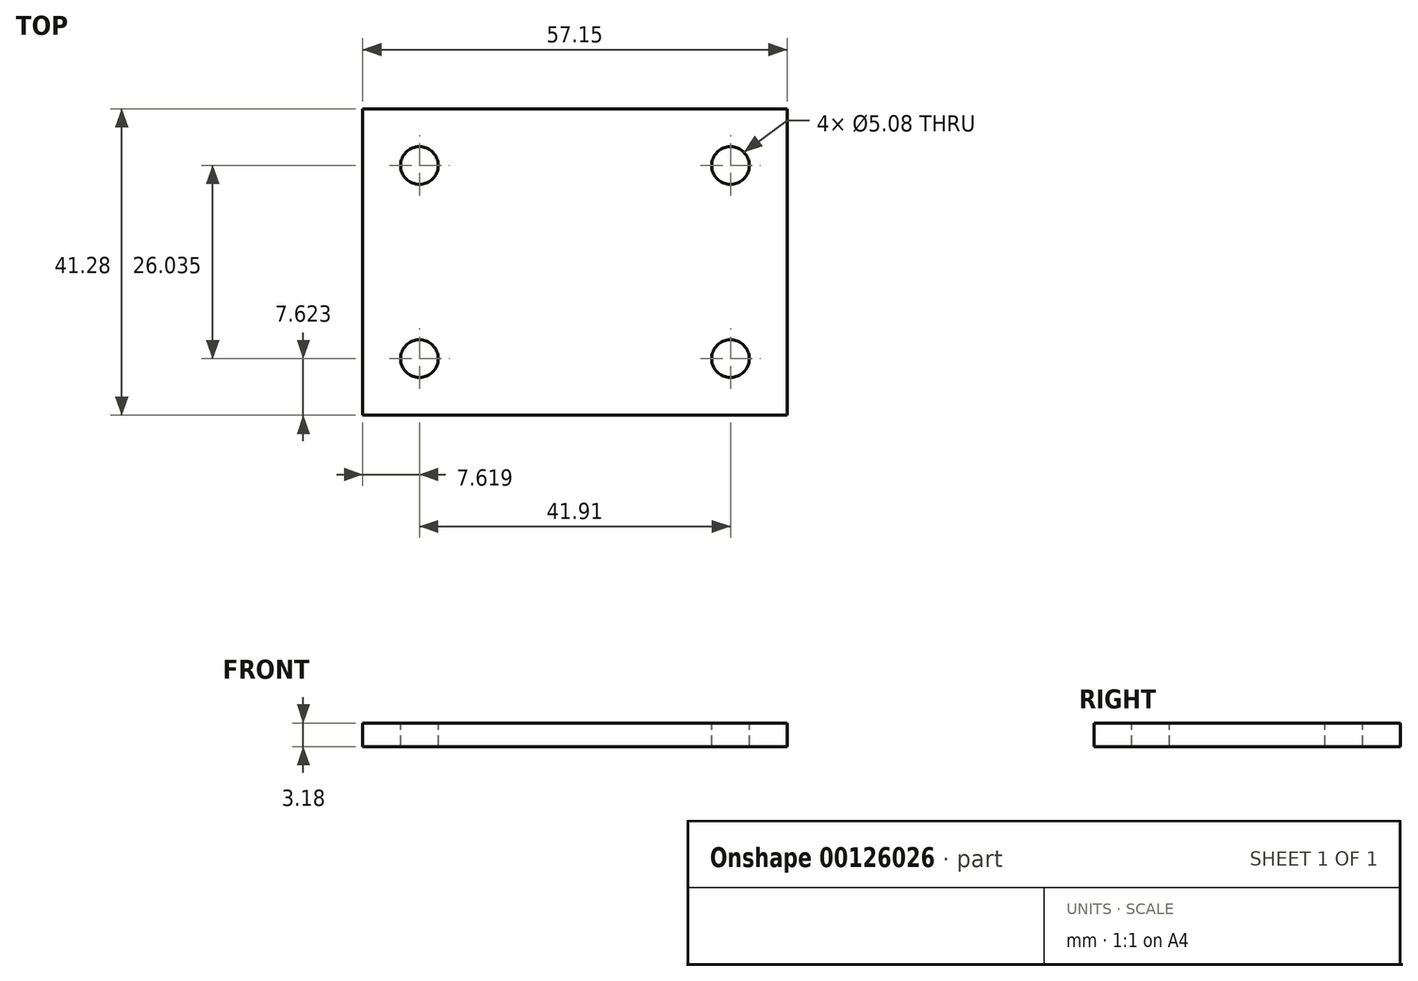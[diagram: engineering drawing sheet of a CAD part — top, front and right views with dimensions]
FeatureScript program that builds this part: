
annotation { "Feature Type Name" : "Feature", "Feature Type Description" : "" }
export const myFeature = defineFeature(function(context is Context, id is Id, definition is map)
    precondition{}
    {
        {
            var Q0;
            Q0=qCreatedBy(makeId("Top.planeOp"),FACE);
            var sketch = newSketch(context, id + "F0", { "sketchPlane" : qUnion([Q0])});
            skLineSegment(sketch, "E0.bottom", {"start": v(-24.2, 2.93) * mm, "end": v(32.96, 2.93) * mm});
            skLineSegment(sketch, "E0.top", {"start": v(-24.2, -38.35) * mm, "end": v(32.96, -38.35) * mm});
            skLineSegment(sketch, "E0.left", {"start": v(-24.2, 2.93) * mm, "end": v(-24.2, -38.35) * mm});
            skLineSegment(sketch, "E0.right", {"start": v(32.96, 2.93) * mm, "end": v(32.96, -38.35) * mm});
            skSolve(sketch);
        }
        {
            var Q0;
            Q0 = qSketchRegion(id + "F0", true);
            extrude(context, id + "F1", {"entities" : qUnion([Q0]), "depth" : 3.17 * mm});
        }
        {
            var Q0;
            Q0=makeQuery(id+"F1.opExtrude","CAP_FACE",FACE,{"disambiguationData":[OSD([sQuery(id+"F0.wireOp",EDGE,"E0.bottom"),sQuery(id+"F0.wireOp",EDGE,"E0.top"),sQuery(id+"F0.wireOp",EDGE,"E0.left"),sQuery(id+"F0.wireOp",EDGE,"E0.right")])],"isStart":false});
            var sketch = newSketch(context, id + "F2", { "sketchPlane" : qUnion([Q0])});
            skLineSegment(sketch, "E1.bottom", {"start": v(-24.2, 2.93) * mm, "end": v(-16.57, 2.93) * mm});
            skLineSegment(sketch, "E1.top", {"start": v(-24.2, -4.7) * mm, "end": v(-16.57, -4.7) * mm});
            skLineSegment(sketch, "E1.left", {"start": v(-24.2, 2.93) * mm, "end": v(-24.2, -4.7) * mm});
            skLineSegment(sketch, "E1.right", {"start": v(-16.57, 2.93) * mm, "end": v(-16.57, -4.7) * mm});
            skLineSegment(sketch, "E2.bottom", {"start": v(32.96, 2.93) * mm, "end": v(25.34, 2.93) * mm});
            skLineSegment(sketch, "E2.top", {"start": v(32.96, -4.7) * mm, "end": v(25.34, -4.7) * mm});
            skLineSegment(sketch, "E2.left", {"start": v(32.96, 2.93) * mm, "end": v(32.96, -4.7) * mm});
            skLineSegment(sketch, "E2.right", {"start": v(25.34, 2.93) * mm, "end": v(25.34, -4.7) * mm});
            skLineSegment(sketch, "E3.bottom", {"start": v(32.96, -38.35) * mm, "end": v(25.34, -38.35) * mm});
            skLineSegment(sketch, "E3.top", {"start": v(32.96, -30.73) * mm, "end": v(25.34, -30.73) * mm});
            skLineSegment(sketch, "E3.left", {"start": v(32.96, -38.35) * mm, "end": v(32.96, -30.73) * mm});
            skLineSegment(sketch, "E3.right", {"start": v(25.34, -38.35) * mm, "end": v(25.34, -30.73) * mm});
            skLineSegment(sketch, "E4.bottom", {"start": v(-24.2, -38.35) * mm, "end": v(-16.57, -38.35) * mm});
            skLineSegment(sketch, "E4.top", {"start": v(-24.2, -30.73) * mm, "end": v(-16.57, -30.73) * mm});
            skLineSegment(sketch, "E4.left", {"start": v(-24.2, -38.35) * mm, "end": v(-24.2, -30.73) * mm});
            skLineSegment(sketch, "E4.right", {"start": v(-16.57, -38.35) * mm, "end": v(-16.57, -30.73) * mm});
            skCircle(sketch, "E5", {"center": v(-16.57, -4.7) * mm, "radius": 2.54 * mm});
            skCircle(sketch, "E6", {"center": v(25.34, -4.7) * mm, "radius": 2.54 * mm});
            skCircle(sketch, "E7", {"center": v(25.34, -30.73) * mm, "radius": 2.54 * mm});
            skCircle(sketch, "E8", {"center": v(-16.57, -30.73) * mm, "radius": 2.54 * mm});
            skSolve(sketch);
        }
        {
            var Q0;
            {var subQ0=sQuery(id+"F2.wireOp",EDGE,"E1.right");var subQ1=sQuery(id+"F2.wireOp",EDGE,"E1.top");var subQ2=makeQuery(id+"F2.imprint","INTERSECT",VERTEX,{"derivedFrom":[subQ1,subQ0]});Q0=makeQuery(id+"F2.imprint","IMPRINT",FACE,{"disambiguationData":[TD([[makeQuery(id+"F2.imprint","IMPRINT",EDGE,{"disambiguationData":[TD([[subQ2,1.0]])],"derivedFrom":subQ1}),1.0]])]});}
            var Q1;
            {var subQ0=sQuery(id+"F2.wireOp",EDGE,"E1.right");var subQ1=sQuery(id+"F2.wireOp",EDGE,"E1.top");var subQ2=makeQuery(id+"F2.imprint","INTERSECT",VERTEX,{"derivedFrom":[subQ1,subQ0]});Q1=makeQuery(id+"F2.imprint","IMPRINT",FACE,{"disambiguationData":[TD([[makeQuery(id+"F2.imprint","IMPRINT",EDGE,{"disambiguationData":[TD([[subQ2,1.0]])],"derivedFrom":subQ1}),-1.0]])]});}
            var Q2;
            {var subQ0=sQuery(id+"F2.wireOp",EDGE,"E2.right");var subQ1=sQuery(id+"F2.wireOp",EDGE,"E2.top");var subQ2=makeQuery(id+"F2.imprint","INTERSECT",VERTEX,{"derivedFrom":[subQ1,subQ0]});Q2=makeQuery(id+"F2.imprint","IMPRINT",FACE,{"disambiguationData":[TD([[makeQuery(id+"F2.imprint","IMPRINT",EDGE,{"disambiguationData":[TD([[subQ2,1.0]])],"derivedFrom":subQ1}),-1.0]])]});}
            var Q3;
            {var subQ0=sQuery(id+"F2.wireOp",EDGE,"E2.right");var subQ1=sQuery(id+"F2.wireOp",EDGE,"E2.top");var subQ2=makeQuery(id+"F2.imprint","INTERSECT",VERTEX,{"derivedFrom":[subQ1,subQ0]});Q3=makeQuery(id+"F2.imprint","IMPRINT",FACE,{"disambiguationData":[TD([[makeQuery(id+"F2.imprint","IMPRINT",EDGE,{"disambiguationData":[TD([[subQ2,1.0]])],"derivedFrom":subQ1}),1.0]])]});}
            var Q4;
            {var subQ0=sQuery(id+"F2.wireOp",EDGE,"E3.right");var subQ1=sQuery(id+"F2.wireOp",EDGE,"E3.top");var subQ2=makeQuery(id+"F2.imprint","INTERSECT",VERTEX,{"derivedFrom":[subQ1,subQ0]});Q4=makeQuery(id+"F2.imprint","IMPRINT",FACE,{"disambiguationData":[TD([[makeQuery(id+"F2.imprint","IMPRINT",EDGE,{"disambiguationData":[TD([[subQ2,1.0]])],"derivedFrom":subQ1}),-1.0]])]});}
            var Q5;
            {var subQ0=sQuery(id+"F2.wireOp",EDGE,"E3.right");var subQ1=sQuery(id+"F2.wireOp",EDGE,"E3.top");var subQ2=makeQuery(id+"F2.imprint","INTERSECT",VERTEX,{"derivedFrom":[subQ1,subQ0]});Q5=makeQuery(id+"F2.imprint","IMPRINT",FACE,{"disambiguationData":[TD([[makeQuery(id+"F2.imprint","IMPRINT",EDGE,{"disambiguationData":[TD([[subQ2,1.0]])],"derivedFrom":subQ1}),1.0]])]});}
            var Q6;
            {var subQ0=sQuery(id+"F2.wireOp",EDGE,"E4.right");var subQ1=sQuery(id+"F2.wireOp",EDGE,"E4.top");var subQ2=makeQuery(id+"F2.imprint","INTERSECT",VERTEX,{"derivedFrom":[subQ1,subQ0]});Q6=makeQuery(id+"F2.imprint","IMPRINT",FACE,{"disambiguationData":[TD([[makeQuery(id+"F2.imprint","IMPRINT",EDGE,{"disambiguationData":[TD([[subQ2,1.0]])],"derivedFrom":subQ1}),-1.0]])]});}
            var Q7;
            {var subQ0=sQuery(id+"F2.wireOp",EDGE,"E4.right");var subQ1=sQuery(id+"F2.wireOp",EDGE,"E4.top");var subQ2=makeQuery(id+"F2.imprint","INTERSECT",VERTEX,{"derivedFrom":[subQ1,subQ0]});Q7=makeQuery(id+"F2.imprint","IMPRINT",FACE,{"disambiguationData":[TD([[makeQuery(id+"F2.imprint","IMPRINT",EDGE,{"disambiguationData":[TD([[subQ2,1.0]])],"derivedFrom":subQ1}),1.0]])]});}
            extrude(context, id + "F3", {"entities" : qUnion([Q0, Q1, Q2, Q3, Q4, Q5, Q6, Q7]), "operationType" : NewBodyOperationType.REMOVE, "oppositeDirection" : true, "depth" : 6.35 * mm});
        }
    });
